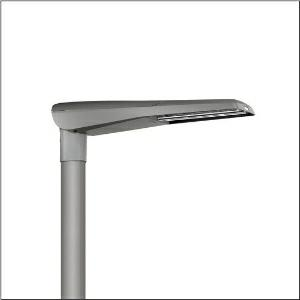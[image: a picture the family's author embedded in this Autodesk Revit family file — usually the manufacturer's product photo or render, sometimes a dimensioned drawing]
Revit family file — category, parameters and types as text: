
# Revit family: streetlight_sl_11_iq_mini___st1_2a_5xc2ac1g08he_29a3
name_source: partatom
category: Lighting Fixtures
units: mm (PartAtom-declared; Revit-internal decimal feet)

## family parameters
Cut with Voids When Loaded = No
Host = Face
Light Source = No
Part Type = Normal
Room Calculation Point = No
Round Connector Dimension = Use Diameter
Shared = No

## types (1)
- --- (1 x LED, 6820 lm, 63.6 W, 2200K)
    Apparent Load = 64 VA
    CIE Flux Codes = 32 70 96 100 100
    Color Rendering = 70
    Color Temperature = 2200K
    Default Elevation = 1800 mm
    Description = Streetlight SL 11 iQ mini, mast luminaire, primary light control with 3 zone facetted reflector, of plastic, silver coated, highly specular, primary optical cover: cover, of PMMA, transparent, light distribution: ST1.2a, light emission: direct distribution, primary light characteristic: asymmetric, installation type: post-top, side-entry, lamps: LED, High Power LED, rated values: 8.330lm | 62,2W | 133,9lm/W (begin service life); end service life: 8.330lm | 65,6W; at 50% lumin. flux: 4.165lm | 29,4W | 141,7lm/W, colour temperature: 2200/2700/3000/4000K, colour rendering: CRI > 70, light colour: 722/727/730/740, light setting 1 begin service life: 100% | 8.330lm | 62,2W | 133,9lm/W | 3.000K, light setting 1 end service life: 65,6W, further light settings possible, control: pre-setting: linear dimming characteristic, Street-Remote, Auto-Match, Temp-Guard, Lumen-Switch, Night-Set, Smart-Wire, Light-Fading, Desk-Remote (wireless, voltage-free reading and setting of iQ features in the workshop via application-optimized NFC function/RFID function), optimised constant luminous flux control (CLO 2.0), with cable H07RN-F 5x 1.5mm², mains connection: 230..240V, AC, 50/60Hz, connection cable pre-assembled, cable length: 8,5m, luminaire housing, of diecast aluminium, powder-coated, Siteco® metallic grey (DB 702S), please order mast flange separately, inclination adjustable without tools: 0°, 5°, 10°, 15° (post-top) | 0°, -5°, -10°, -15° (side-entry), sealing non-destructively replaceable, multi-level sealing system, length: 736mm, width: 174mm, height: 116mm, mast flange for spigot size: 42mm (side-entry): 5XC10008XM4, 60/48mm (side-entry/post-top): 5XC10108XM2, 76/60mm (side-entry/post-top): 5XC10108XM1, equipment: Power, protection rating (complete): IP66, insulation class (complete): insulation class II (safety insulation), certification: CE, ENEC, ENEC+, VDE, impact resistance: IK10, permissible operating ambient temperature for outdoor applications: -25..+50°C, standard-compliant lighting for roads and squares, Environmental Product Declaration (EPD) tested and certified by an independent institute, packaging unit: 1 piece

Light Distribution: ST1.2a
    Height = 116 mm
    Lamp = 1 x LED
    Lamp Light Flux = 6820 lm
    Lamp Power = 63.6 W
    Lamp count = 1
    Length = 736 mm
    Luminous efficacy = 107 lm/W
    Manufacturer = Siteco
    ModVariant = No
    Model = 5XC2AC1G08HE
    Number of Poles = 1
    OnlyDefault = Yes
    Power Factor = 1
    Product Name = Streetlight SL 11 iQ mini | ST1.2a
    Product group = mast luminaire | pylon top
    ProductGroupID = 6100
    Protection Class = Protection class II
    Protection Degree = IP 66
    RLX_Detail_Level = 1
    RLX_Emergency_Light_Flux = 0 lm
    RLX_Emergency_Type = 0
    RLX_Emergency_Type_DB = No
    RlxData = <blob elided: 53677 chars, md5=2c4d98fb>
    Socket = socket
    Standby Power = 0 W
    System Light Flux = 6820 lm
    System Power = 64 W
    Type Comments = individual setting: luminous flux: 100 % | dim-lin: 254 | 866 mA
    Type Image = l_1003508.jpg
    URL = http://relux.com
    VarID = @adj_055037
    Voltage = 0 V
    Weight = 0.00 kg
    Width = 174 mm

## geometry (parser evidence)
native form markers: Blend x4, Sweep x10
no freeform markers — native parametric forms only
